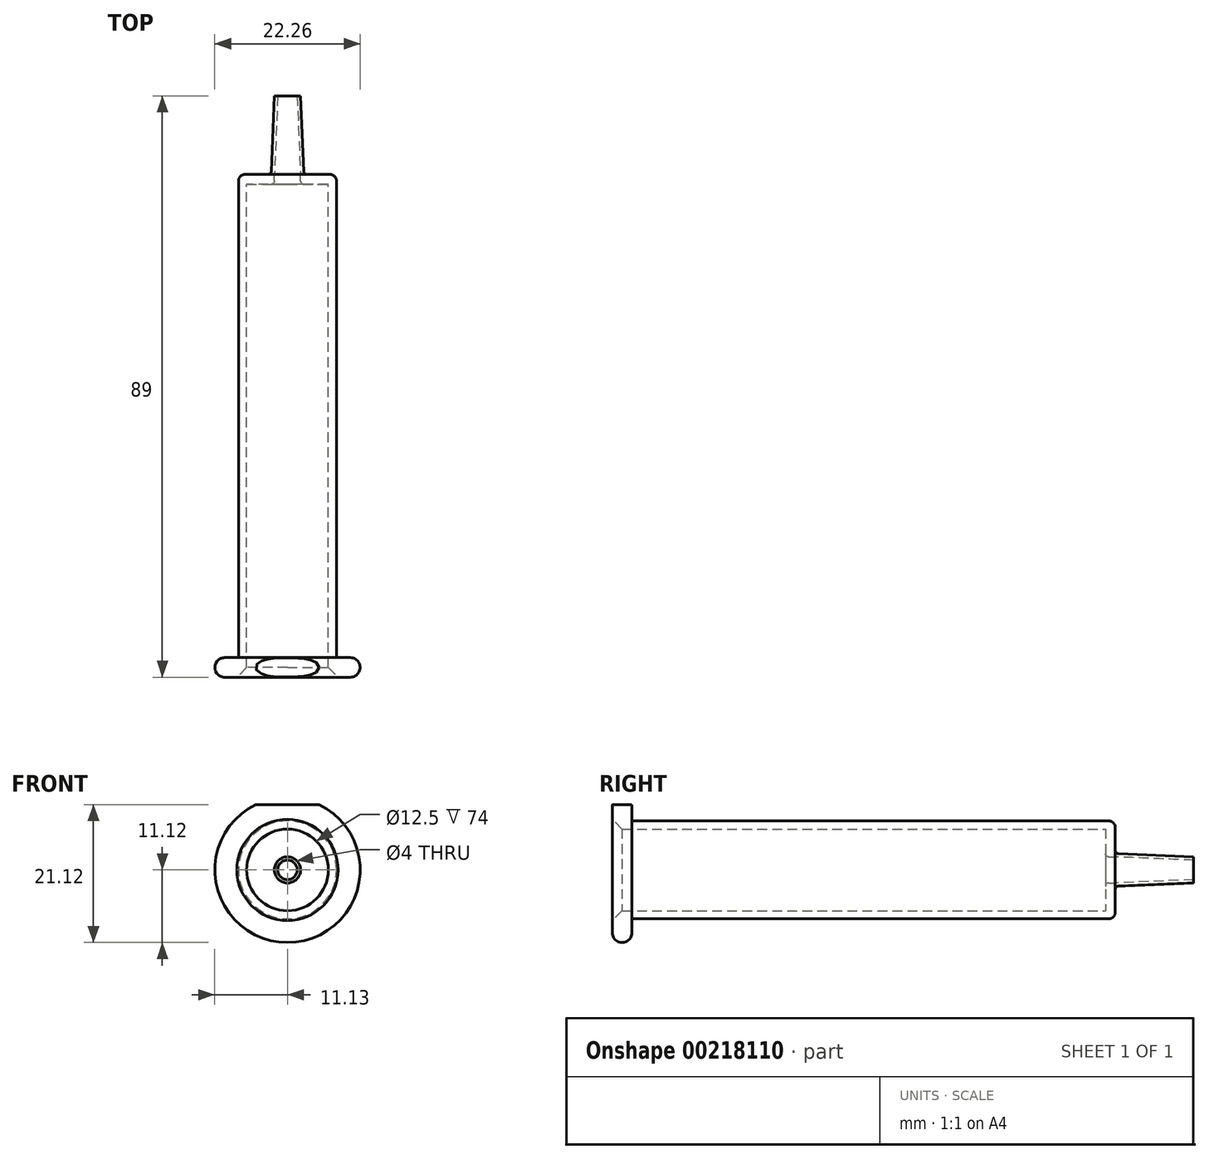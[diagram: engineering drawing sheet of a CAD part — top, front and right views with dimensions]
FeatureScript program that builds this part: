
annotation { "Feature Type Name" : "Feature", "Feature Type Description" : "" }
export const myFeature = defineFeature(function(context is Context, id is Id, definition is map)
    precondition{}
    {
        {
            var Q0;
            Q0=qCreatedBy(makeId("Front.planeOp"),FACE);
            var sketch = newSketch(context, id + "F0", { "sketchPlane" : qUnion([Q0])});
            skCircle(sketch, "E0", {"center": v(0, 0) * mm, "radius": 7.5 * mm});
            skCircle(sketch, "E1", {"center": v(0, 0) * mm, "radius": 6.25 * mm});
            skSolve(sketch);
        }
        {
            var Q0;
            Q0=makeQuery(id+"F0.imprint","IMPRINT",FACE,{"disambiguationData":[TD([[makeQuery(id+"F0.imprint","IMPRINT",EDGE,{"derivedFrom":sQuery(id+"F0.wireOp",EDGE,"E0")}),1.0]])]});
            extrude(context, id + "F1", {"entities" : qUnion([Q0]), "depth" : 77 * mm});
        }
        {
            var Q0;
            Q0=makeQuery(id+"F1.opExtrude","CAP_FACE",FACE,{"disambiguationData":[OSD([sQuery(id+"F0.wireOp",EDGE,"E0"),sQuery(id+"F0.wireOp",EDGE,"E1")])],"isStart":false});
            var sketch = newSketch(context, id + "F2", { "sketchPlane" : qUnion([Q0])});
            skCircle(sketch, "E2", {"center": v(0, 0) * mm, "radius": 6.25 * mm});
            skCircle(sketch, "E3", {"center": v(0, 0) * mm, "radius": 11.12 * mm});
            skSolve(sketch);
        }
        {
            var Q0;
            Q0=makeQuery(id+"F2.imprint","IMPRINT",FACE,{"disambiguationData":[TD([[makeQuery(id+"F2.imprint","IMPRINT",EDGE,{"derivedFrom":sQuery(id+"F2.wireOp",EDGE,"E3")}),1.0]])]});
            var Q1;
            Q1=makeQuery(id+"F2.imprint","IMPRINT",FACE,{"disambiguationData":[TD([[makeQuery(id+"F2.imprint","IMPRINT",EDGE,{"derivedFrom":sQuery(id+"F2.wireOp",EDGE,"E2")}),-1.0]])]});
            extrude(context, id + "F3", {"entities" : qUnion([Q0, Q1]), "operationType" : NewBodyOperationType.ADD, "oppositeDirection" : true, "depth" : 3 * mm});
        }
        {
            var Q0;
            Q0=makeQuery(id+"F3.opExtrude","CAP_EDGE",EDGE,{"disambiguationData":[OSD([sQuery(id+"F2.wireOp",EDGE,"E3")])],"isStart":true});
            var Q1;
            Q1=makeQuery(id+"F3.opExtrude","CAP_EDGE",EDGE,{"disambiguationData":[OSD([sQuery(id+"F2.wireOp",EDGE,"E3")])],"isStart":false});
            fillet(context, id + "F4", {"entities" : qUnion([Q0, Q1]), "radius" : 1.5 * mm, "tangentPropagation" : true, "allowEdgeOverflow" : false});
        }
        {
            var Q0;
            Q0=makeQuery(id+"F3.boolean.opBoolean","MERGE",FACE,{"derivedFrom":[makeQuery(id+"F1.opExtrude","CAP_FACE",FACE,{"disambiguationData":[OSD([sQuery(id+"F0.wireOp",EDGE,"E0"),sQuery(id+"F0.wireOp",EDGE,"E1")])],"isStart":false}),makeQuery(id+"F3.opExtrude","CAP_FACE",FACE,{"disambiguationData":[OSD([sQuery(id+"F2.wireOp",EDGE,"E2"),sQuery(id+"F2.wireOp",EDGE,"E3")])],"isStart":true})]});
            var sketch = newSketch(context, id + "F5", { "sketchPlane" : qUnion([Q0])});
            skLineSegment(sketch, "E4", {"start": v(-10.21, 10) * mm, "end": v(17.5, 10) * mm});
            skLineSegment(sketch, "E5", {"start": v(-10.21, 10) * mm, "end": v(-7.58, 15.42) * mm});
            skLineSegment(sketch, "E6", {"start": v(17.5, 10) * mm, "end": v(14.55, 16.55) * mm});
            skLineSegment(sketch, "E7", {"start": v(14.55, 16.55) * mm, "end": v(-7.58, 15.42) * mm});
            skSolve(sketch);
        }
        {
            var Q0;
            Q0=makeQuery(id+"F5.imprint","IMPRINT",FACE,{"disambiguationData":[TD([[makeQuery(id+"F5.imprint","IMPRINT",EDGE,{"derivedFrom":sQuery(id+"F5.wireOp",EDGE,"E4")}),1.0]])]});
            extrude(context, id + "F6", {"entities" : qUnion([Q0]), "operationType" : NewBodyOperationType.REMOVE, "oppositeDirection" : true, "depth" : 25 * mm});
        }
        {
            var Q0;
            Q0=makeQuery(id+"F1.opExtrude","CAP_EDGE",EDGE,{"disambiguationData":[OSD([sQuery(id+"F0.wireOp",EDGE,"E1")])],"isStart":false});
            chamfer(context, id + "F7", {"entities" : qUnion([Q0]), "width" : 1.5 * mm, "tangentPropagation" : true});
        }
        {
            var Q0;
            Q0=makeQuery(id+"F1.opExtrude","CAP_FACE",FACE,{"disambiguationData":[OSD([sQuery(id+"F0.wireOp",EDGE,"E0"),sQuery(id+"F0.wireOp",EDGE,"E1")])],"isStart":true});
            var sketch = newSketch(context, id + "F8", { "sketchPlane" : qUnion([Q0])});
            skCircle(sketch, "E8", {"center": v(0, 0) * mm, "radius": 7.5 * mm});
            skSolve(sketch);
        }
        {
            var Q0;
            Q0=qSketchRegion(id+"F8",true);
            extrude(context, id + "F9", {"entities" : qUnion([Q0]), "operationType" : NewBodyOperationType.ADD, "oppositeDirection" : true, "depth" : 1.5 * mm});
        }
        {
            var Q0;
            Q0=makeQuery(id+"F1.opExtrude","CAP_EDGE",EDGE,{"disambiguationData":[OSD([sQuery(id+"F0.wireOp",EDGE,"E0")])],"isStart":true});
            fillet(context, id + "F10", {"entities" : qUnion([Q0]), "radius" : 1 * mm, "tangentPropagation" : true, "allowEdgeOverflow" : false});
        }
        {
            var Q0;
            Q0=qCreatedBy(makeId("Right.planeOp"),FACE);
            var sketch = newSketch(context, id + "F11", { "sketchPlane" : qUnion([Q0])});
            skLineSegment(sketch, "E9", {"start": v(0, -2.5) * mm, "end": v(12, -2) * mm});
            skLineSegment(sketch, "E10", {"start": v(0, -2.5) * mm, "end": v(0, -2) * mm});
            skLineSegment(sketch, "E11", {"start": v(12, -2) * mm, "end": v(12, -1.5) * mm});
            skLineSegment(sketch, "E12", {"start": v(12, -1.5) * mm, "end": v(0, -2) * mm});
            skLineSegment(sketch, "E13", {"start": v(19.59, 0) * mm, "end": v(-9.42, 0) * mm, "construction": true});
            skSolve(sketch);
        }
        {
            var Q0;
            Q0=makeQuery(id+"F11.imprint","IMPRINT",FACE,{"disambiguationData":[TD([[makeQuery(id+"F11.imprint","IMPRINT",EDGE,{"derivedFrom":sQuery(id+"F11.wireOp",EDGE,"E9")}),1.0]])]});
            var Q1;
            Q1=sQuery(id+"F11.wireOp",EDGE,"E13");
            revolve(context, id + "F12", {"operationType" : NewBodyOperationType.ADD, "entities" : qUnion([Q0]), "axis" : qUnion([Q1]), "revolveType" : RevolveType.FULL});
        }
        {
            var Q0;
            Q0=makeQuery(id+"F12.opRevolve","SWEPT_EDGE",EDGE,{"disambiguationData":[OSD([sQuery(id+"F11.wireOp",EDGE,"E9"),sQuery(id+"F11.wireOp",EDGE,"E10")])]});
            fillet(context, id + "F13", {"entities" : qUnion([Q0]), "radius" : .5 * mm, "tangentPropagation" : true, "allowEdgeOverflow" : false});
        }
        {
            var Q0;
            {var subQ0=sQuery(id+"F0.wireOp",EDGE,"E0");Q0=makeQuery(id+"F12.boolean.opBoolean","SPLIT",FACE,{"disambiguationData":[TD([makeQuery(id+"F10.opFillet","BLEND_FACE",FACE,{"disambiguationData":[OSD([subQ0])]})])],"derivedFrom":makeQuery(id+"F9.boolean.opBoolean","MERGE",FACE,{"derivedFrom":[makeQuery(id+"F1.opExtrude","CAP_FACE",FACE,{"disambiguationData":[OSD([subQ0,sQuery(id+"F0.wireOp",EDGE,"E1")])],"isStart":true}),makeQuery(id+"F9.opExtrude","CAP_FACE",FACE,{"disambiguationData":[OSD([sQuery(id+"F8.wireOp",EDGE,"E8")])],"isStart":true})]})});}
            var sketch = newSketch(context, id + "F14", { "sketchPlane" : qUnion([Q0])});
            skCircle(sketch, "E14", {"center": v(0, 0) * mm, "radius": 2 * mm});
            skSolve(sketch);
        }
        {
            var Q0;
            Q0=makeQuery(id+"F14.imprint","IMPRINT",FACE,{"disambiguationData":[TD([[makeQuery(id+"F14.imprint","IMPRINT",EDGE,{"derivedFrom":sQuery(id+"F14.wireOp",EDGE,"E14")}),1.0]])]});
            extrude(context, id + "F15", {"entities" : qUnion([Q0]), "operationType" : NewBodyOperationType.REMOVE, "oppositeDirection" : true, "depth" : 25 * mm});
        }
        {
            var Q0;
            Q0=makeQuery(id+"F15.boolean.opBoolean","INTERSECT",EDGE,{"derivedFrom":[makeQuery(id+"F9.opExtrude","CAP_FACE",FACE,{"disambiguationData":[OSD([sQuery(id+"F8.wireOp",EDGE,"E8")])],"isStart":false}),makeQuery(id+"F15.opExtrude","SWEPT_FACE",FACE,{"disambiguationData":[OSD([sQuery(id+"F14.wireOp",EDGE,"E14")])]})]});
            fillet(context, id + "F16", {"entities" : qUnion([Q0]), "radius" : .5 * mm, "tangentPropagation" : true, "allowEdgeOverflow" : false});
        }
    });
